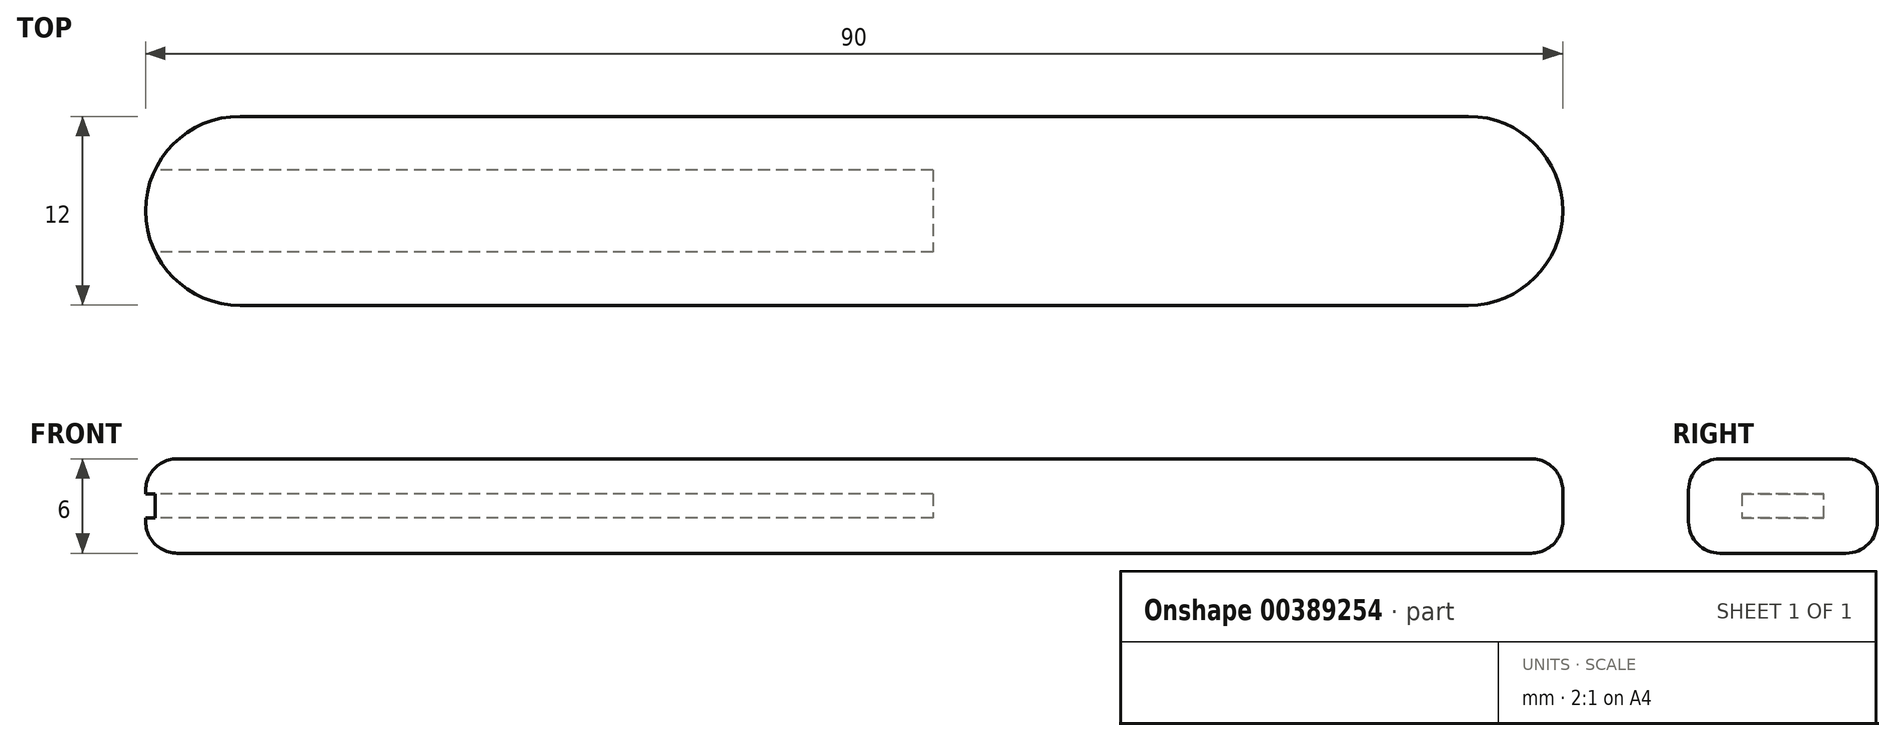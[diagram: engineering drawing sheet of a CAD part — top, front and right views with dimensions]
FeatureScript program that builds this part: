
annotation { "Feature Type Name" : "Feature", "Feature Type Description" : "" }
export const myFeature = defineFeature(function(context is Context, id is Id, definition is map)
    precondition{}
    {
        {
            var Q0;
            Q0=qCreatedBy(makeId("Top.planeOp"),FACE);
            var sketch = newSketch(context, id + "F0", { "sketchPlane" : qUnion([Q0])});
            skLineSegment(sketch, "E0.bottom", {"start": v(33.5, -8) * mm, "end": v(-56.5, -8) * mm});
            skLineSegment(sketch, "E0.top", {"start": v(33.5, 4) * mm, "end": v(-56.5, 4) * mm});
            skLineSegment(sketch, "E0.left", {"start": v(33.5, -8) * mm, "end": v(33.5, 4) * mm});
            skLineSegment(sketch, "E0.right", {"start": v(-56.5, -8) * mm, "end": v(-56.5, 4) * mm});
            skSolve(sketch);
        }
        {
            var Q0;
            Q0 = qSketchRegion(id + "F0", true);
            extrude(context, id + "F1", {"entities" : qUnion([Q0]), "depth" : 6 * mm, "offsetDistance" : 25 * mm});
        }
        {
            var Q0;
            Q0=makeQuery(id+"F1.opExtrude","SWEPT_FACE",FACE,{"disambiguationData":[OSD([sQuery(id+"F0.wireOp",EDGE,"E0.right")])]});
            var sketch = newSketch(context, id + "F2", { "sketchPlane" : qUnion([Q0])});
            skLineSegment(sketch, "E1.bottom", {"start": v(-0.6, 3.75) * mm, "end": v(4.6, 3.75) * mm});
            skLineSegment(sketch, "E1.top", {"start": v(-0.6, 2.25) * mm, "end": v(4.6, 2.25) * mm});
            skLineSegment(sketch, "E1.left", {"start": v(-0.6, 3.75) * mm, "end": v(-0.6, 2.25) * mm});
            skLineSegment(sketch, "E1.right", {"start": v(4.6, 3.75) * mm, "end": v(4.6, 2.25) * mm});
            skLineSegment(sketch, "E2", {"start": v(-0.6, 3) * mm, "end": v(4.6, 3) * mm, "construction": true});
            skLineSegment(sketch, "E3", {"start": v(2, 3.75) * mm, "end": v(2, 2.25) * mm, "construction": true});
            skSolve(sketch);
        }
        {
            var Q0;
            Q0 = qSketchRegion(id + "F2", true);
            extrude(context, id + "F3", {"entities" : qUnion([Q0]), "operationType" : NewBodyOperationType.REMOVE, "oppositeDirection" : true, "depth" : 50 * mm, "offsetDistance" : 25 * mm});
        }
        {
            var Q0;
            Q0=makeQuery(id+"F1.opExtrude","SWEPT_EDGE",EDGE,{"disambiguationData":[OSD([sQuery(id+"F0.wireOp",EDGE,"E0.bottom"),sQuery(id+"F0.wireOp",EDGE,"E0.right")])]});
            var Q1;
            Q1=makeQuery(id+"F1.opExtrude","SWEPT_EDGE",EDGE,{"disambiguationData":[OSD([sQuery(id+"F0.wireOp",EDGE,"E0.top"),sQuery(id+"F0.wireOp",EDGE,"E0.right")])]});
            var Q2;
            Q2=makeQuery(id+"F1.opExtrude","SWEPT_EDGE",EDGE,{"disambiguationData":[OSD([sQuery(id+"F0.wireOp",EDGE,"E0.bottom"),sQuery(id+"F0.wireOp",EDGE,"E0.left")])]});
            var Q3;
            Q3=makeQuery(id+"F1.opExtrude","SWEPT_EDGE",EDGE,{"disambiguationData":[OSD([sQuery(id+"F0.wireOp",EDGE,"E0.top"),sQuery(id+"F0.wireOp",EDGE,"E0.left")])]});
            fillet(context, id + "F4", {"entities" : qUnion([Q0, Q1, Q2, Q3]), "radius" : 6 * mm, "tangentPropagation" : true, "defaultsChanged" : true, "vertexSettings" : [], "allowEdgeOverflow" : false});
        }
        {
            var Q0;
            Q0=makeQuery(id+"F1.opExtrude","CAP_EDGE",EDGE,{"disambiguationData":[OSD([sQuery(id+"F0.wireOp",EDGE,"E0.bottom")])],"isStart":false});
            var Q1;
            Q1=makeQuery(id+"F1.opExtrude","CAP_EDGE",EDGE,{"disambiguationData":[OSD([sQuery(id+"F0.wireOp",EDGE,"E0.bottom")])],"isStart":true});
            fillet(context, id + "F5", {"entities" : qUnion([Q0, Q1]), "radius" : 2 * mm, "tangentPropagation" : true, "defaultsChanged" : true, "vertexSettings" : [], "allowEdgeOverflow" : false});
        }
    });
